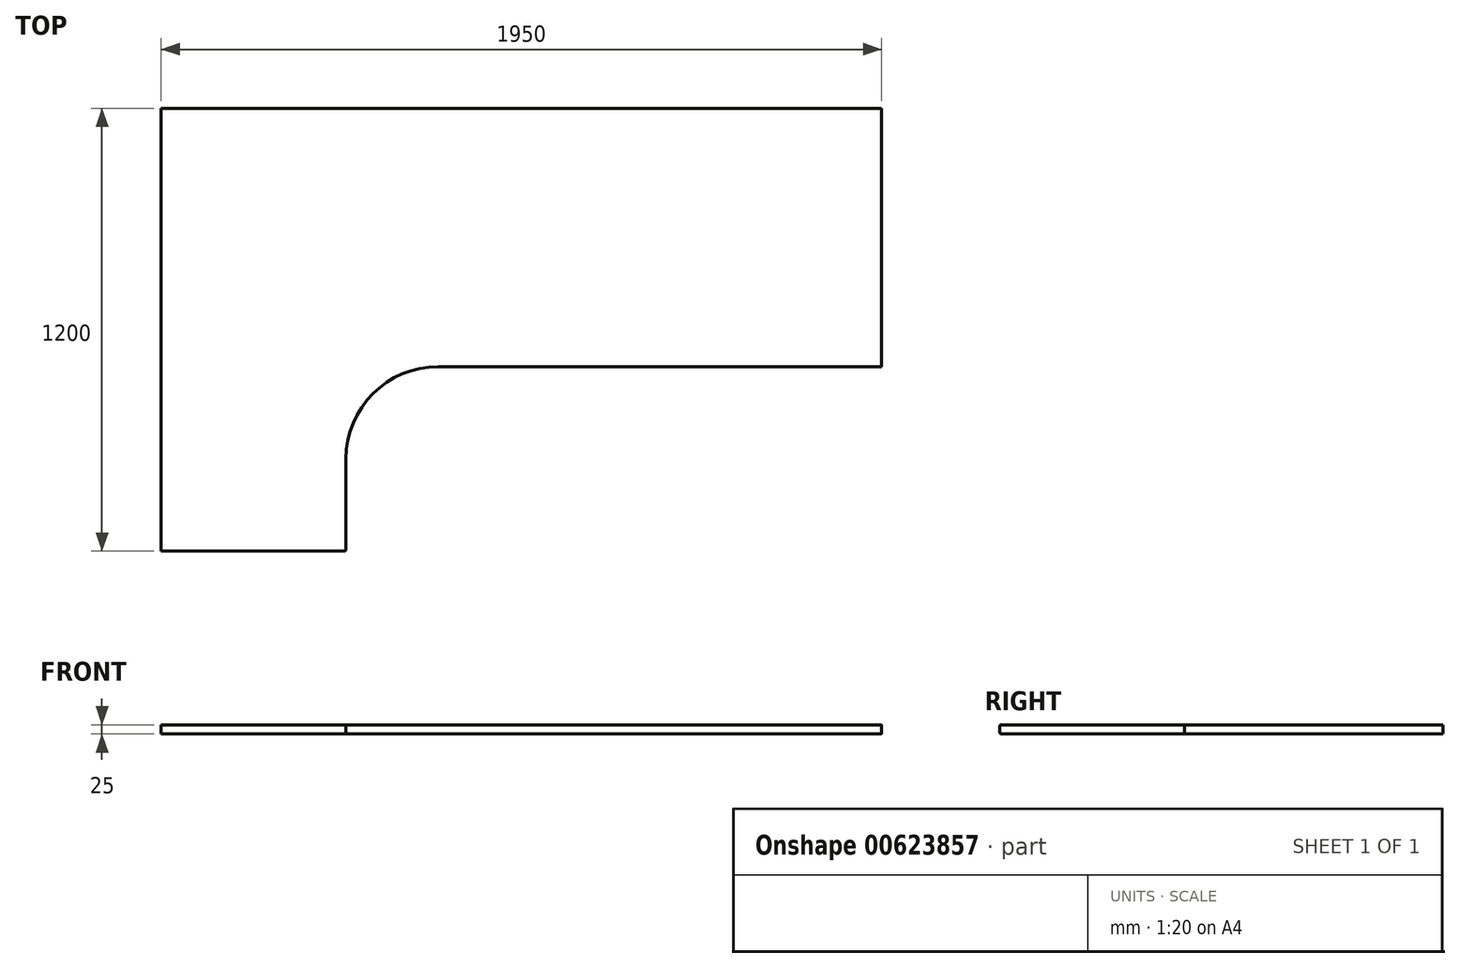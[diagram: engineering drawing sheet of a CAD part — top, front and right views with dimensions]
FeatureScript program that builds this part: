
annotation { "Feature Type Name" : "Feature", "Feature Type Description" : "" }
export const myFeature = defineFeature(function(context is Context, id is Id, definition is map)
    precondition{}
    {
        {
            var Q0;
            Q0=qCreatedBy(makeId("Top.planeOp"),FACE);
            var sketch = newSketch(context, id + "F0", { "sketchPlane" : qUnion([Q0])});
            skLineSegment(sketch, "E0", {"start": v(0, -1200) * mm, "end": v(0, 0) * mm});
            skLineSegment(sketch, "E1", {"start": v(0, 0) * mm, "end": v(1950, 0) * mm});
            skLineSegment(sketch, "E2", {"start": v(1950, 0) * mm, "end": v(1950, -700) * mm});
            skLineSegment(sketch, "E3", {"start": v(1950, -700) * mm, "end": v(750, -700) * mm});
            skLineSegment(sketch, "E4", {"start": v(0, -1200) * mm, "end": v(500, -1200) * mm});
            skLineSegment(sketch, "E5", {"start": v(500, -1200) * mm, "end": v(500, -950) * mm});
            skArc(sketch, "E6", {"start": v(750, -700) * mm, "mid": v(573.22, -773.22) * mm, "end": v(500, -950) * mm});
            skSolve(sketch);
        }
        {
            var Q0;
            Q0 = qSketchRegion(id + "F0", true);
            extrude(context, id + "F1", {"entities" : qUnion([Q0]), "depth" : 25 * mm, "offsetDistance" : 25 * mm});
        }
        {
            var Q0;
            Q0=makeQuery(id+"F1.opExtrude","CAP_EDGE",EDGE,{"disambiguationData":[OSD([sQuery(id+"F0.wireOp",EDGE,"E3")])],"isStart":false});
            var Q1;
            Q1=makeQuery(id+"F1.opExtrude","CAP_EDGE",EDGE,{"disambiguationData":[OSD([sQuery(id+"F0.wireOp",EDGE,"E3")])],"isStart":true});
            var Q2;
            Q2=makeQuery(id+"F1.opExtrude","CAP_EDGE",EDGE,{"disambiguationData":[OSD([sQuery(id+"F0.wireOp",EDGE,"E4")])],"isStart":false});
            var Q3;
            Q3=makeQuery(id+"F1.opExtrude","CAP_EDGE",EDGE,{"disambiguationData":[OSD([sQuery(id+"F0.wireOp",EDGE,"E4")])],"isStart":true});
            var Q4;
            Q4=makeQuery(id+"F1.opExtrude","SWEPT_EDGE",EDGE,{"disambiguationData":[OSD([sQuery(id+"F0.wireOp",EDGE,"E4"),sQuery(id+"F0.wireOp",EDGE,"E5")])]});
            fillet(context, id + "F2", {"entities" : qUnion([Q0, Q1, Q2, Q3, Q4]), "radius" : 5 * mm, "tangentPropagation" : true, "allowEdgeOverflow" : false});
        }
    });
